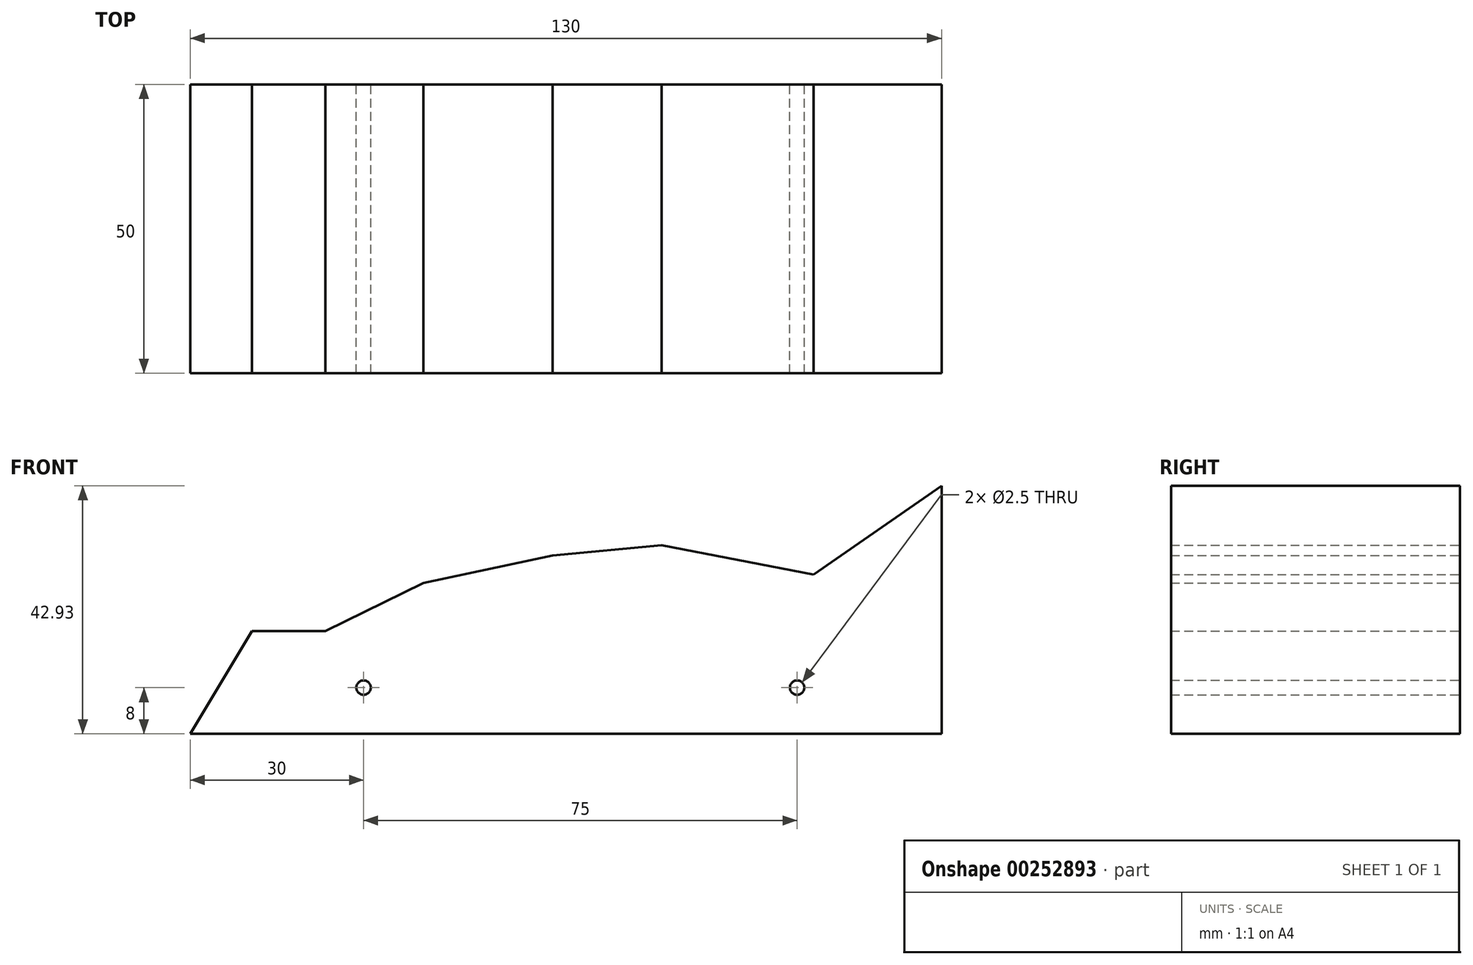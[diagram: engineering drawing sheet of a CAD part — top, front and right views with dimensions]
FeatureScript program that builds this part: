
annotation { "Feature Type Name" : "Feature", "Feature Type Description" : "" }
export const myFeature = defineFeature(function(context is Context, id is Id, definition is map)
    precondition{}
    {
        {
            var Q0;
            Q0=qCreatedBy(makeId("Front.planeOp"),FACE);
            var sketch = newSketch(context, id + "F0", { "sketchPlane" : qUnion([Q0])});
            skLineSegment(sketch, "E0.bottom", {"start": v(50, -25) * mm, "end": v(-50, -25) * mm});
            skLineSegment(sketch, "E0.top", {"start": v(50, 25) * mm, "end": v(-50, 25) * mm});
            skLineSegment(sketch, "E0.left", {"start": v(50, -25) * mm, "end": v(50, 25) * mm});
            skPoint(sketch, "E0.middle", {"position": v(0, 0) * mm});
            skLineSegment(sketch, "E1", {"start": v(-50, -25) * mm, "end": v(-80, -25) * mm});
            skLineSegment(sketch, "E2", {"start": v(-50, 25) * mm, "end": v(-80, -25) * mm});
            skLineSegment(sketch, "E3", {"start": v(50, -25) * mm, "end": v(25, -25) * mm});
            skLineSegment(sketch, "E4", {"start": v(25, -18.25) * mm, "end": v(25, -17) * mm});
            skLineSegment(sketch, "E5", {"start": v(-50, -18.25) * mm, "end": v(-50, -17) * mm});
            skCircle(sketch, "E6", {"center": v(-50, -17) * mm, "radius": 1.25 * mm});
            skCircle(sketch, "E7", {"center": v(25, -17) * mm, "radius": 1.25 * mm});
            skLineSegment(sketch, "E8", {"start": v(-64.34, 1.1) * mm, "end": v(-39.64, 1.1) * mm});
            skLineSegment(sketch, "E9", {"start": v(-39.64, 1.1) * mm, "end": v(-17.28, 5.87) * mm});
            skLineSegment(sketch, "E10", {"start": v(-17.28, 5.87) * mm, "end": v(1.58, 7.62) * mm});
            skLineSegment(sketch, "E11", {"start": v(1.58, 7.62) * mm, "end": v(27.83, 2.57) * mm});
            skLineSegment(sketch, "E12", {"start": v(27.83, 2.57) * mm, "end": v(50, 17.93) * mm});
            skLineSegment(sketch, "E13", {"start": v(-39.64, 1.1) * mm, "end": v(-56.63, -7.2) * mm});
            skLineSegment(sketch, "E14", {"start": v(-56.63, -7.2) * mm, "end": v(-68.41, -5.69) * mm});
            skLineSegment(sketch, "E15", {"start": v(-68.41, -5.69) * mm, "end": v(-56.63, -7.2) * mm});
            skLineSegment(sketch, "E16", {"start": v(-69.32, -7.2) * mm, "end": v(-56.63, -7.2) * mm});
            skSolve(sketch);
        }
        {
            var Q0;
            Q0=makeQuery(id+"F0.imprint","IMPRINT",FACE,{"disambiguationData":[TD([[makeQuery(id+"F0.imprint","IMPRINT",EDGE,{"derivedFrom":sQuery(id+"F0.wireOp",EDGE,"E0.bottom")}),-1.0]])]});
            extrude(context, id + "F1", {"entities" : qUnion([Q0]), "depth" : 50 * mm});
        }
    });
